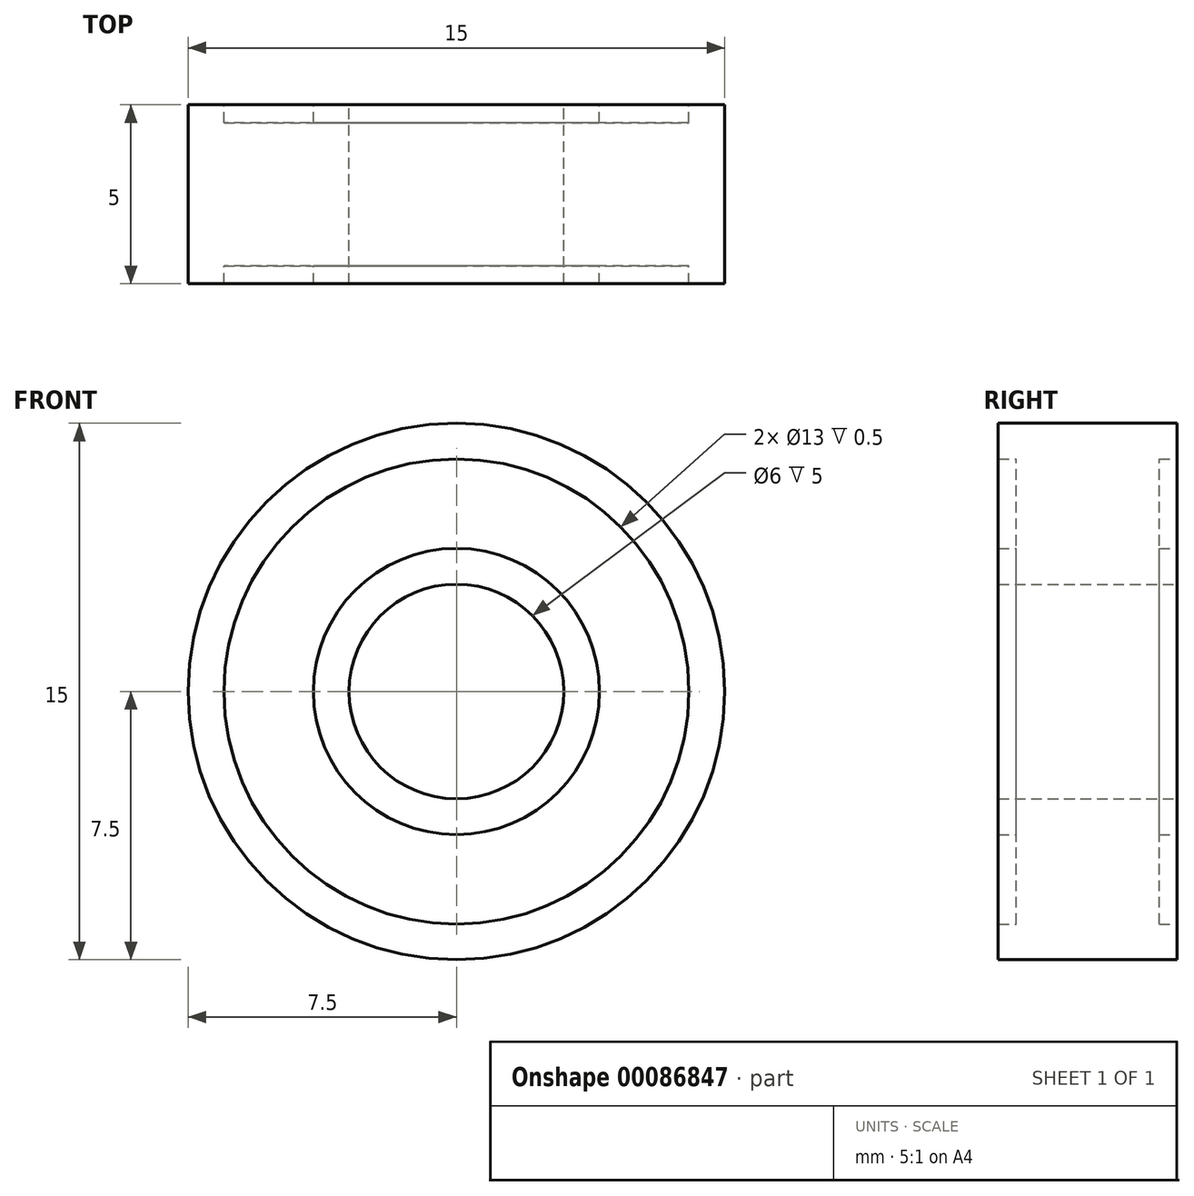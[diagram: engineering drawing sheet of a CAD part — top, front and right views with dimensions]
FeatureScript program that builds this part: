
annotation { "Feature Type Name" : "Feature", "Feature Type Description" : "" }
export const myFeature = defineFeature(function(context is Context, id is Id, definition is map)
    precondition{}
    {
        {
            var Q0;
            Q0=qCreatedBy(makeId("Front.planeOp"),FACE);
            var sketch = newSketch(context, id + "F0", { "sketchPlane" : qUnion([Q0])});
            skCircle(sketch, "E0", {"center": v(0, 0) * mm, "radius": 7.5 * mm});
            skCircle(sketch, "E1", {"center": v(0, 0) * mm, "radius": 6.5 * mm});
            skCircle(sketch, "E2", {"center": v(0, 0) * mm, "radius": 4 * mm});
            skCircle(sketch, "E3", {"center": v(0, 0) * mm, "radius": 3 * mm});
            skSolve(sketch);
        }
        {
            var Q0;
            Q0=makeQuery(id+"F0.imprint","IMPRINT",FACE,{"disambiguationData":[TD([[makeQuery(id+"F0.imprint","IMPRINT",EDGE,{"derivedFrom":sQuery(id+"F0.wireOp",EDGE,"E0")}),1.0]])]});
            extrude(context, id + "F1", {"entities" : qUnion([Q0]), "depth" : 5 * mm, "symmetric" : true});
        }
        {
            var Q0;
            Q0=makeQuery(id+"F0.imprint","IMPRINT",FACE,{"disambiguationData":[TD([[makeQuery(id+"F0.imprint","IMPRINT",EDGE,{"derivedFrom":sQuery(id+"F0.wireOp",EDGE,"E1")}),1.0]])]});
            extrude(context, id + "F2", {"entities" : qUnion([Q0]), "operationType" : NewBodyOperationType.ADD, "depth" : 4 * mm, "symmetric" : true});
        }
        {
            var Q0;
            Q0=makeQuery(id+"F0.imprint","IMPRINT",FACE,{"disambiguationData":[TD([[makeQuery(id+"F0.imprint","IMPRINT",EDGE,{"derivedFrom":sQuery(id+"F0.wireOp",EDGE,"E2")}),1.0]])]});
            extrude(context, id + "F3", {"entities" : qUnion([Q0]), "operationType" : NewBodyOperationType.ADD, "depth" : 5 * mm, "symmetric" : true});
        }
    });
